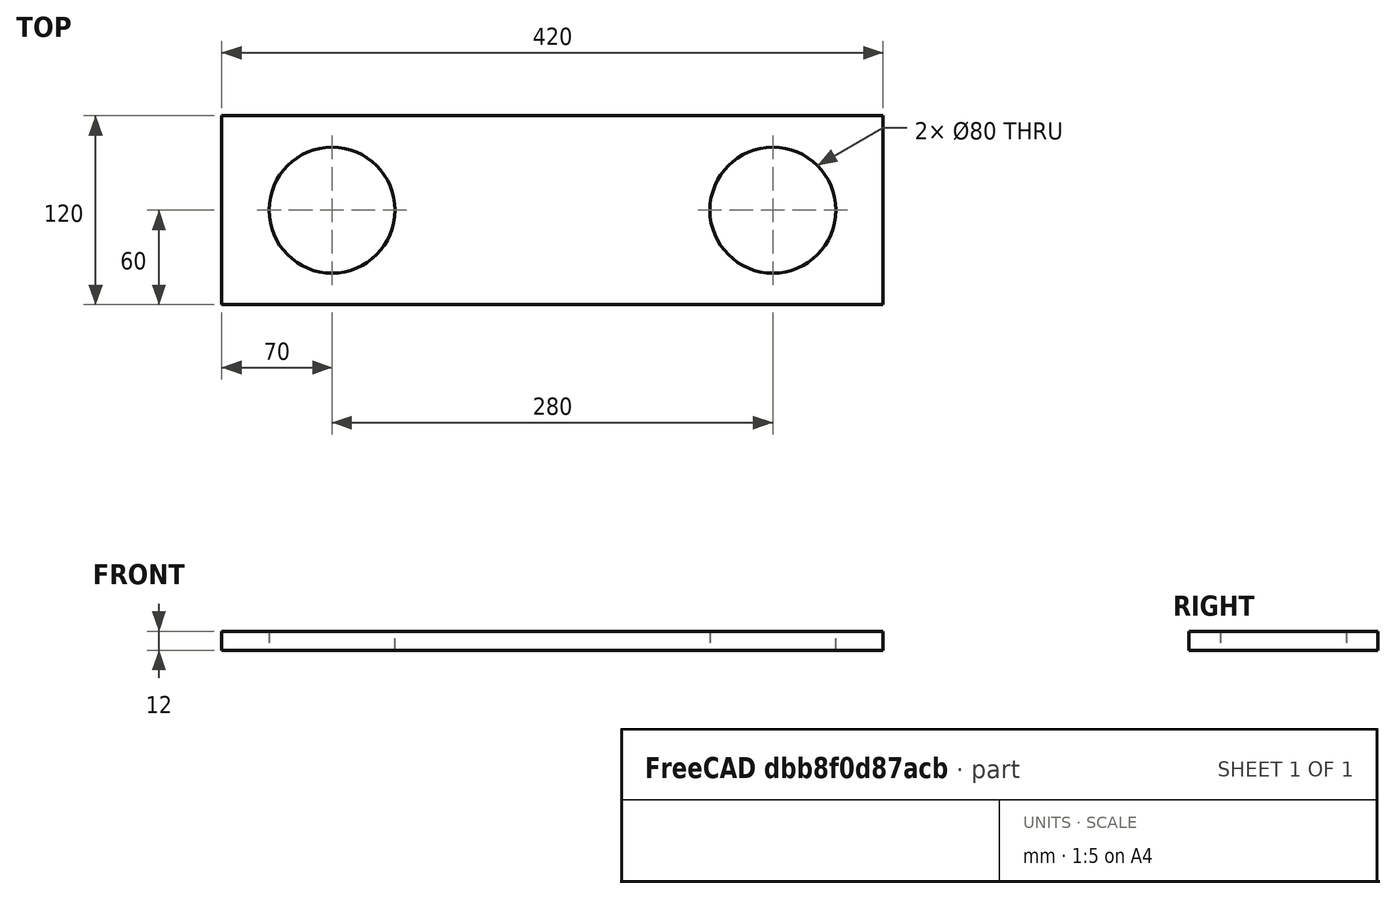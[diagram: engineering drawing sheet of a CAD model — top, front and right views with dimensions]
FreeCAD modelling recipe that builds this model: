
FCSTD DOCUMENT  (FreeCAD 0.18R16131 (Git))
Label: Speaker_plate
License: All rights reserved
LicenseURL: http://en.wikipedia.org/wiki/All_rights_reserved
objects: Sketcher::SketchObject×1, PartDesign::Pad×1, PartDesign::Body×1
note: 4 computed .brp shape members not serialized (recipe doc carries the construction recipe); baked Part::Feature solids carry a one-line shape summary decoded from their .brp

FEATURE [Sketcher::SketchObject] Sketch
  MapMode = 5
  Support = -> [XY_Plane]
  sketch-geometry (10):
    g0: LineSegment StartX=0 StartY=0 StartZ=0 EndX=420 EndY=0 EndZ=0
    g1: LineSegment StartX=420 StartY=0 StartZ=0 EndX=420 EndY=-120 EndZ=0
    g2: LineSegment StartX=420 StartY=-120 StartZ=0 EndX=0 EndY=-120 EndZ=0
    g3: LineSegment StartX=0 StartY=-120 StartZ=0 EndX=0 EndY=0 EndZ=0
    g4: Circle CenterX=70 CenterY=-60 CenterZ=0 NormalX=0 NormalY=0 NormalZ=1 AngleXU=0 Radius=40
    g5: Circle CenterX=350 CenterY=-60 CenterZ=0 NormalX=0 NormalY=0 NormalZ=1 AngleXU=0 Radius=40
    g6: LineSegment [constr] StartX=70 StartY=-60 StartZ=0 EndX=210 EndY=-60 EndZ=0
    g7: LineSegment [constr] StartX=210 StartY=-60 StartZ=0 EndX=350 EndY=-60 EndZ=0
    g8: LineSegment [constr] StartX=210 StartY=-60 StartZ=0 EndX=0 EndY=-7.1e-15 EndZ=0
    g9: LineSegment [constr] StartX=210 StartY=-60 StartZ=0 EndX=420 EndY=-120 EndZ=0
  constraints (26):
    c: Coincident(g0,g1)
    c: Coincident(g1,g2)
    c: Coincident(g2,g3)
    c: Coincident(g3,g0)
    c: Horizontal(g0)
    c: Horizontal(g2)
    c: Vertical(g3)
    c: Coincident(g0,g-1)
    c: DistanceX(g0,g0) = 420
    c: DistanceY(g3,g3) = 120
    c: Horizontal(g4,g5)
    c: Equal(g4,g5)
    c: Radius(g4) = 40
    c: Vertical(g1)
    c: Coincident(g6,g4)
    c: Horizontal(g6)
    c: Coincident(g7,g6)
    c: Coincident(g7,g5)
    c: Equal(g6,g7)
    c: Coincident(g8,g6)
    c: Coincident(g8,g0)
    c: Coincident(g9,g6)
    c: Coincident(g9,g1)
    c: Parallel(g9,g8)
    c: Equal(g9,g8)
    c: DistanceX(g6,g6) = 140
FEATURE [PartDesign::Pad] Pad
  Length = 12
  Length2 = 100
  Profile = -> Sketch
  Type = 0
FEATURE [PartDesign::Body] Body
  Group = -> [Sketch,Pad]
  Origin = -> Origin
  Tip = -> Pad
